# Revit family: Haworth_XSeries_PersonalStorageTower_24Wide3High
name_source: partatom
category: Furniture Systems
units: mm (PartAtom-declared; Revit-internal decimal feet)

## family parameters
Always vertical = Yes
Cut with Voids When Loaded = No
OmniClass Number = 23.40.70.14.64.21
OmniClass Title = Systems Furniture
Part Type = Normal
Room Calculation Point = No
Round Connector Dimension = Use Diameter
Shared = No
Work Plane-Based = No

## types (1)
- 24d 24w 40h - Upper Door - Box File
    Actual Depth = 23 5/8"
    Actual Height = 40 1/2"
    Actual Width = 24"
    Assembly Code = E2020200
    Caster Offset = 0"
    Classic Pull = No
    Crescent Pull = No
    Description = Haworth XSeries Personal Storage Tower
    Door Height = 37 1/8"
    Door Height 2 = 17 9/16"
    Door Width = 9"
    Drawer 1 Height = 12"
    Drawer 2 Height = 5 15/16"
    Drawer Width = 14 7/8"
    Ellipse Pull = No
    J Pull = No
    Linear Pull = Yes
    Manufacturer = Haworth
    Model = J2HQ-4024
    Pull Finish = Haworth _ Metal _ Brushed Aluminum
    Pull Height Centerline = 30 1/8"
    Pull Height Centerline 2 = 10 9/16"
    Radius Pull = No
    Revision Number = 2
    Shelf Depth = 13 1/2"
    Shelf Width = 22 1/8"
    Size = Verify Final Dim. w/ Haworth
    Standard Heights = 40.5 in.
    Sustainability Info = https://www.haworth.com
    Taper Pull = No
    Top Height = 19 1/16"
    URL = http://www.haworth.com
    URL - Product = https://www.haworth.com
    Warranty = https://cdn.shopify.com

## geometry (parser evidence)
native form markers: Sweep x12
no freeform markers — native parametric forms only
